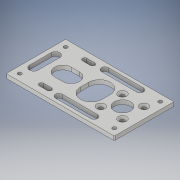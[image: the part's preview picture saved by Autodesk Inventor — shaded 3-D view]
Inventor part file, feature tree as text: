
AUTODESK INVENTOR PART (.ipt)
format: ipt  version: 2018 (Build 220112000, 112)  size: 189,440 bytes
history: native  units: in
note: dims shown in document units (in); Inventor stores cm internally (conversion verified against a paired STEP export)
features: extrude x1, sketch x1, fillet x1
ambient origin geometry x8: Origin, YZ Plane, XZ Plane, XY Plane, X Axis, Y Axis, Z Axis, Center Point
bodies: Solid1 (feature_tree)
feature tree (3):
  extrude  "Extrusion1"  Depth=0.1875in TaperAngle=0.0deg
  sketch  "Sketch1"  dims[d0=0.17in d1=0.1875in d2=0.0in]
  fillet  "Fillet1"  [1 undecoded]
note: 1 required parameter value undecoded (feature->parameter linkage not recoverable at this tier; creation-order binding heuristic only, values carry confidence <= 0.55)
